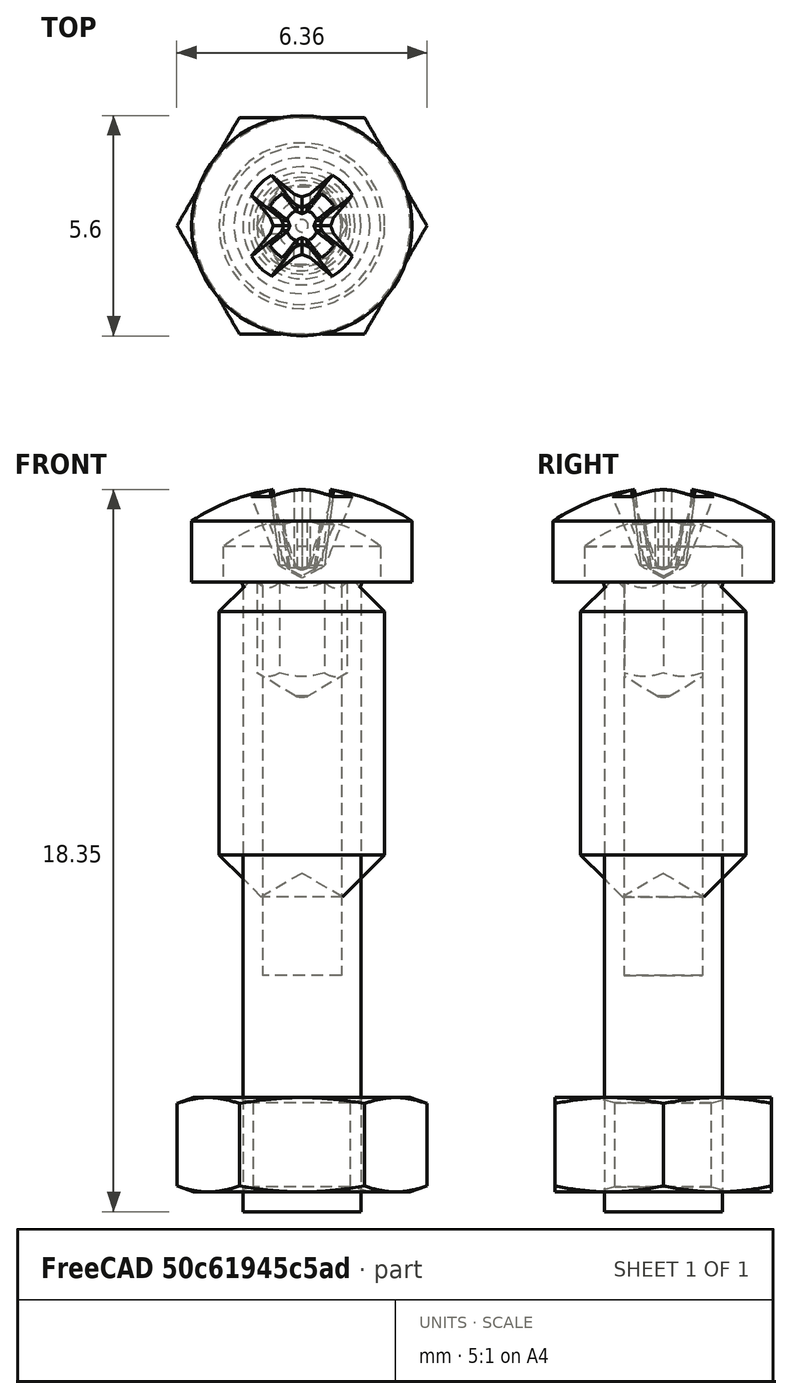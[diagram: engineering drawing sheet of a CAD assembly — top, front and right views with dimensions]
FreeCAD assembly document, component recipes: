
FREECAD ASSEMBLY — COMPONENT RECIPES ("AssemblySteeringL")

This assembly document has 3 components, labeled P0..P2 below (a component is one placed body or linked part). 0 of them carry a construction recipe — the FreeCAD feature program that regenerates the part from scratch, quoted from this document or its linked companion documents; the rest are supplied as boundary geometry only. No exploded tour is included for this assembly.
COMPONENT P0 — geometry summary ("Fastener"; no construction recipe available for this part):
  bounding box: 18.3 x 6.4 x 5.6 mm
  tessellated surface: 650 triangles
  volume: 154 mm^3 (24% of its bounding box)
  symmetry: 2-fold rotationally symmetric about the z axis; mirror-symmetric across its x mid-plane, y mid-plane
COMPONENT P1 — geometry summary ("Screw001"; no construction recipe available for this part):
  bounding box: 8.0 x 4.2 x 4.2 mm
  tessellated surface: 624 triangles
  volume: 51448214072405317586726842617523246409701801578241926693856012274526793496783273013037526060875382784 mm^3 (36331428390073380270083490842798330897472130793162059181908745951797020999246250966536796376708153344% of its bounding box)
  symmetry: mirror-symmetric across its x mid-plane, y mid-plane
COMPONENT P2 — geometry summary ("Screw002"; no construction recipe available for this part):
  bounding box: 11.6 x 4.0 x 4.0 mm
  tessellated surface: 366 triangles
  volume: 16510015933861410385479415748070778212074537923396722840017396173271647356517726568705243494391742464 mm^3 (8920973911852432552025575774956397504777157573574563184746481327183297916750923746073923579048624128% of its bounding box)
  symmetry: 4-fold rotationally symmetric about the z axis; mirror-symmetric across its x mid-plane, y mid-plane
PROVENANCE & LICENSES
A FreeCAD (.FCStd) document from a public repository crawl; recipes are the document's own serialized feature recipes (and, for linked parts, companion documents' recipes).
License: mit.
